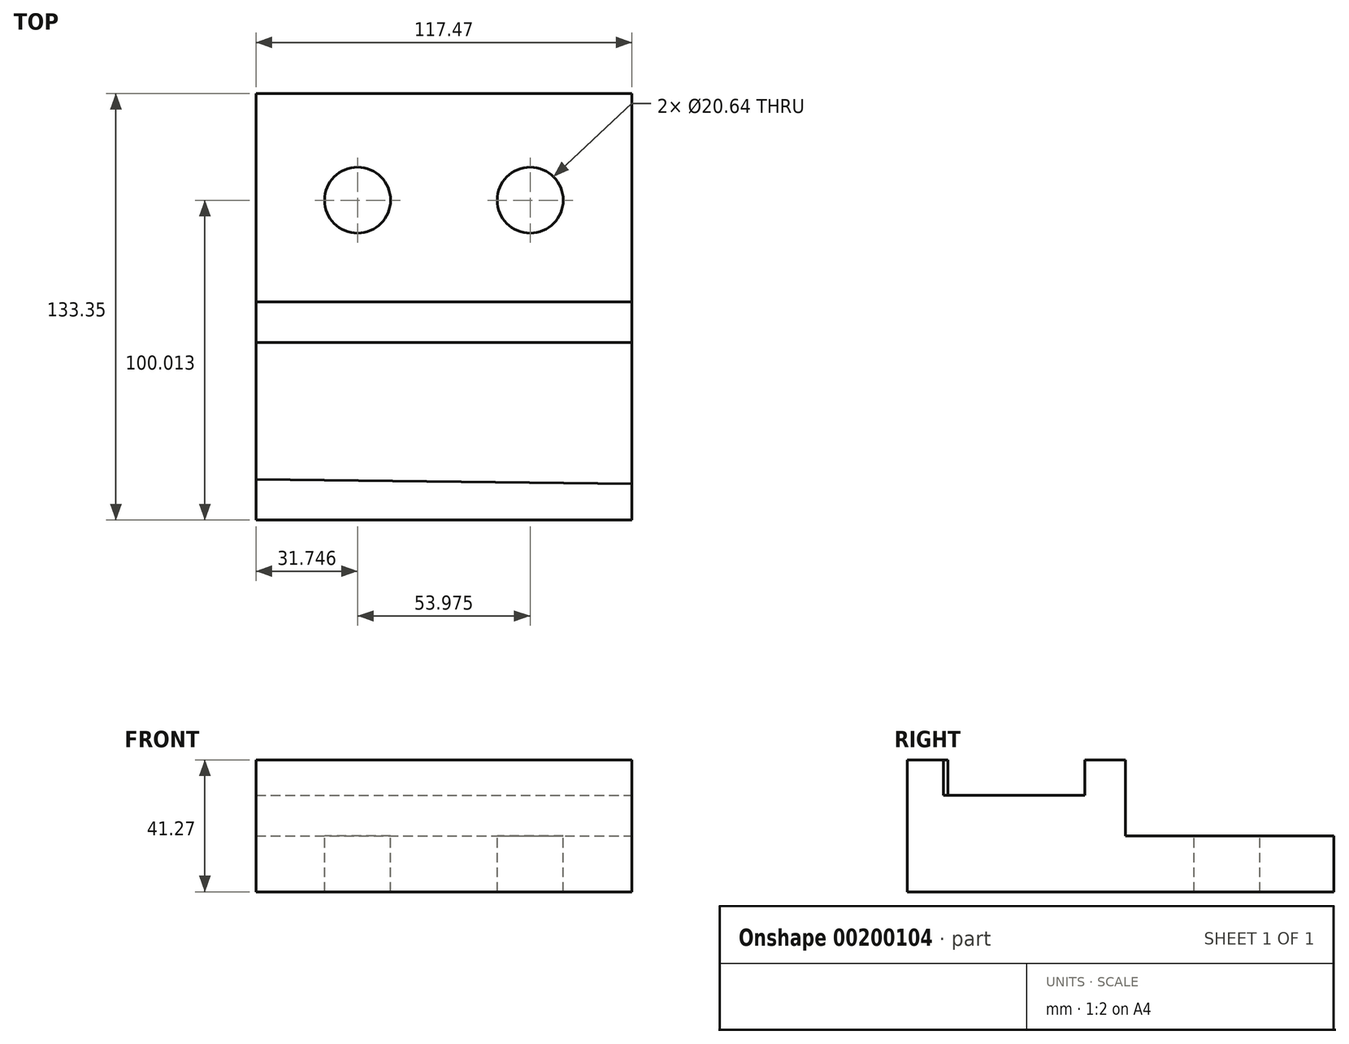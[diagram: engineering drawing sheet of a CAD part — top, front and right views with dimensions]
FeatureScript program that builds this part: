
annotation { "Feature Type Name" : "Feature", "Feature Type Description" : "" }
export const myFeature = defineFeature(function(context is Context, id is Id, definition is map)
    precondition{}
    {
        {
            var Q0;
            Q0=qCreatedBy(makeId("Top.planeOp"),FACE);
            var sketch = newSketch(context, id + "F0", { "sketchPlane" : qUnion([Q0])});
            skLineSegment(sketch, "E0", {"start": v(-94.65, -71.27) * mm, "end": v(-94.65, 62.08) * mm});
            skLineSegment(sketch, "E1", {"start": v(-94.65, 62.08) * mm, "end": v(22.82, 62.08) * mm});
            skLineSegment(sketch, "E2", {"start": v(22.82, 62.08) * mm, "end": v(22.82, -71.27) * mm});
            skLineSegment(sketch, "E3", {"start": v(-94.65, -71.27) * mm, "end": v(22.82, -71.27) * mm});
            skSolve(sketch);
        }
        {
            var Q0;
            Q0=makeQuery(id+"F0.imprint","IMPRINT",FACE,{"disambiguationData":[TD([[makeQuery(id+"F0.imprint","IMPRINT",EDGE,{"derivedFrom":sQuery(id+"F0.wireOp",EDGE,"E0")}),-1.0]])]});
            extrude(context, id + "F1", {"entities" : qUnion([Q0]), "depth" : 17.46 * mm});
        }
        {
            var Q0;
            Q0=makeQuery(id+"F1.opExtrude","CAP_FACE",FACE,{"disambiguationData":[OSD([sQuery(id+"F0.wireOp",EDGE,"E0"),sQuery(id+"F0.wireOp",EDGE,"E1"),sQuery(id+"F0.wireOp",EDGE,"E2"),sQuery(id+"F0.wireOp",EDGE,"E3")])],"isStart":false});
            var sketch = newSketch(context, id + "F2", { "sketchPlane" : qUnion([Q0])});
            skPoint(sketch, "E4", {"position": v(-62.9, 62.08) * mm});
            skPoint(sketch, "E5", {"position": v(-8.93, 62.08) * mm});
            skPoint(sketch, "E6", {"position": v(-94.65, 28.74) * mm});
            skPoint(sketch, "E7", {"position": v(22.82, 28.74) * mm});
            skPoint(sketch, "E8", {"position": v(-8.93, 28.74) * mm});
            skPoint(sketch, "E9", {"position": v(-62.9, 28.74) * mm});
            skCircle(sketch, "E10", {"center": v(-62.9, 28.74) * mm, "radius": 10.33 * mm});
            skCircle(sketch, "E11", {"center": v(-8.93, 28.74) * mm, "radius": 10.32 * mm});
            skPoint(sketch, "E12", {"position": v(-94.65, -3) * mm});
            skPoint(sketch, "E13", {"position": v(22.82, -3) * mm});
            skLineSegment(sketch, "E14", {"start": v(-94.65, -3) * mm, "end": v(22.82, -3) * mm});
            skSolve(sketch);
        }
        {
            var Q0;
            Q0=sQuery(id+"F2.wireOp",VERTEX,"E9");
            var Q1;
            Q1=sQuery(id+"F2.wireOp",VERTEX,"E8");
            var Q2;
            Q2=makeQuery(id+"F1.opExtrude","SWEPT_BODY",BODY,{"disambiguationData":[OSD([sQuery(id+"F0.wireOp",EDGE,"E0"),sQuery(id+"F0.wireOp",EDGE,"E1"),sQuery(id+"F0.wireOp",EDGE,"E2"),sQuery(id+"F0.wireOp",EDGE,"E3")])]});
            hole(context, id + "F3", {"style" : HoleStyle.SIMPLE, "endStyle" : HoleEndStyle.THROUGH, "holeDiameter" : 20.64 * mm, "locations" : qUnion([Q0, Q1]), "scope" : qUnion([Q2]), "isTappedThrough" : true});
        }
        {
            var Q0;
            {var subQ0=sQuery(id+"F2.wireOp",EDGE,"E14");Q0=makeQuery(id+"F2.imprint","IMPRINT",FACE,{"disambiguationData":[TD([[makeQuery(id+"F2.imprint","IMPRINT",EDGE,{"derivedFrom":subQ0}),-1.0]])]});}
            extrude(context, id + "F4", {"entities" : qUnion([Q0]), "operationType" : NewBodyOperationType.ADD, "depth" : 12.7 * mm});
        }
        {
            var Q0;
            Q0=makeQuery(id+"F4.opExtrude","CAP_FACE",FACE,{"disambiguationData":[OSD([sQuery(id+"F0.wireOp",EDGE,"E0"),sQuery(id+"F0.wireOp",EDGE,"E2"),sQuery(id+"F0.wireOp",EDGE,"E3"),sQuery(id+"F2.wireOp",EDGE,"E14")])],"isStart":false});
            var sketch = newSketch(context, id + "F5", { "sketchPlane" : qUnion([Q0])});
            skPoint(sketch, "E15", {"position": v(-94.65, -15.7) * mm});
            skPoint(sketch, "E16", {"position": v(-94.65, -58.57) * mm});
            skPoint(sketch, "E17", {"position": v(22.82, -58.57) * mm});
            skPoint(sketch, "E18", {"position": v(22.82, -15.7) * mm});
            skLineSegment(sketch, "E19", {"start": v(-94.65, -15.7) * mm, "end": v(22.82, -15.7) * mm});
            skLineSegment(sketch, "E20", {"start": v(22.82, -3) * mm, "end": v(-94.65, -3) * mm});
            skLineSegment(sketch, "E21", {"start": v(-94.65, -15.7) * mm, "end": v(-94.65, -3) * mm});
            skLineSegment(sketch, "E22", {"start": v(22.82, -15.7) * mm, "end": v(22.82, -3) * mm});
            skLineSegment(sketch, "E23", {"start": v(22.82, -71.27) * mm, "end": v(22.82, -58.57) * mm});
            skLineSegment(sketch, "E24", {"start": v(-94.65, -58.57) * mm, "end": v(22.82, -59.9) * mm});
            skLineSegment(sketch, "E25", {"start": v(-94.65, -71.27) * mm, "end": v(-94.65, -58.57) * mm});
            skLineSegment(sketch, "E26", {"start": v(-94.65, -71.27) * mm, "end": v(22.82, -71.27) * mm});
            skSolve(sketch);
        }
        {
            var Q0;
            Q0=makeQuery(id+"F5.imprint","IMPRINT",FACE,{"disambiguationData":[TD([[makeQuery(id+"F5.imprint","IMPRINT",EDGE,{"derivedFrom":sQuery(id+"F5.wireOp",EDGE,"E19")}),1.0]])]});
            var Q1;
            {var subQ2=sQuery(id+"F5.wireOp",EDGE,"E24");Q1=makeQuery(id+"F5.imprint","IMPRINT",FACE,{"disambiguationData":[TD([[makeQuery(id+"F5.imprint","IMPRINT",EDGE,{"derivedFrom":subQ2}),-1.0]])]});}
            extrude(context, id + "F6", {"entities" : qUnion([Q0, Q1]), "operationType" : NewBodyOperationType.ADD, "depth" : 11.1 * mm});
        }
    });
